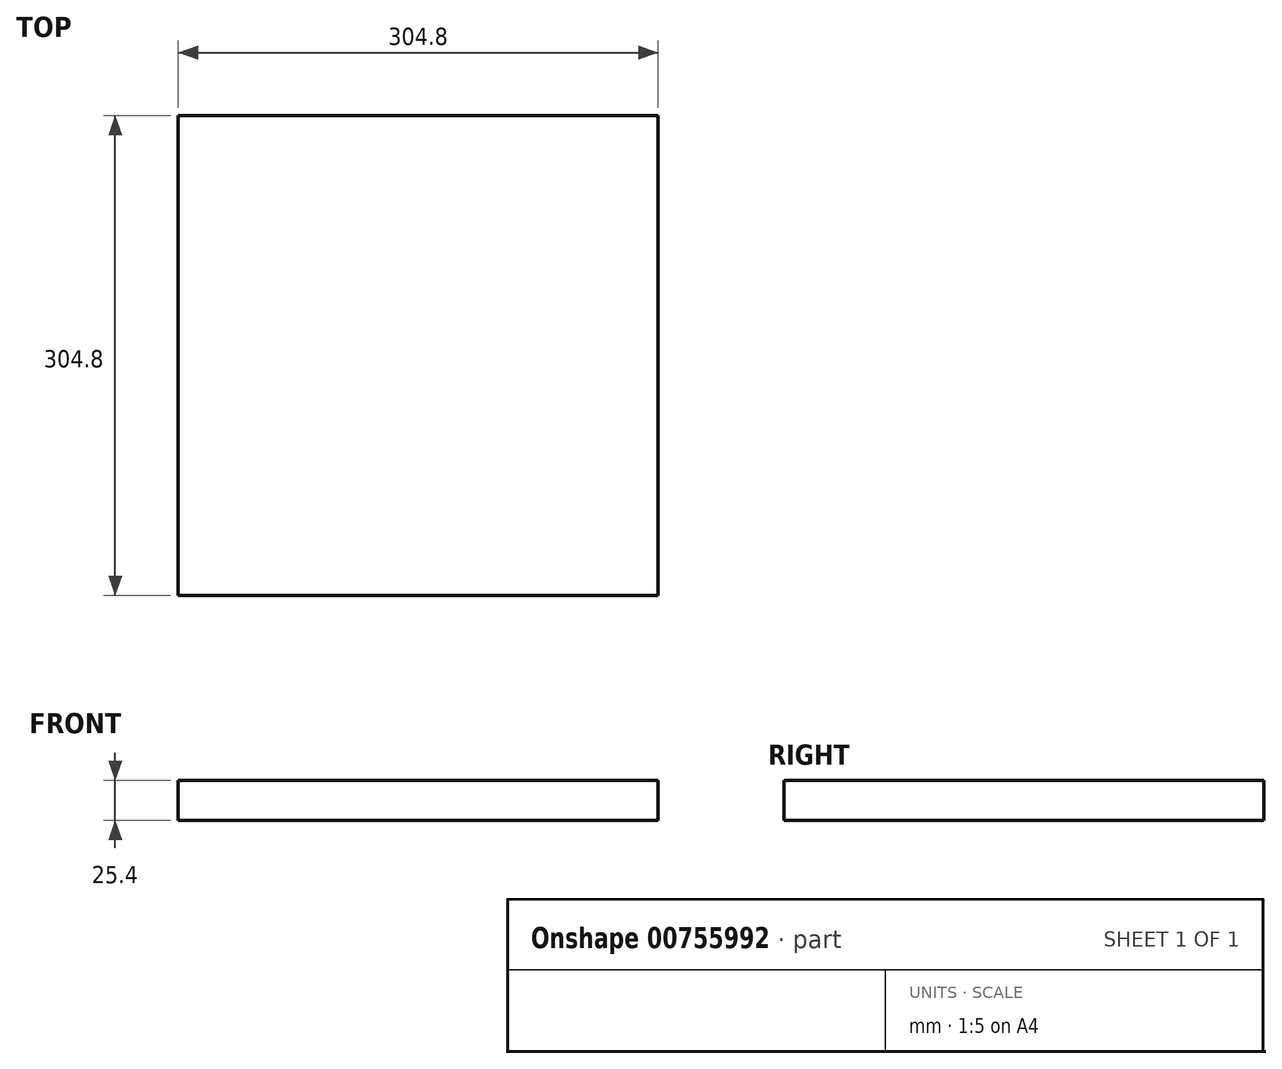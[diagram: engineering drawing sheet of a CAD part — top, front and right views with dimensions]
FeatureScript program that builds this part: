
annotation { "Feature Type Name" : "Feature", "Feature Type Description" : "" }
export const myFeature = defineFeature(function(context is Context, id is Id, definition is map)
    precondition{}
    {
        {
            var Q0;
            Q0=qCreatedBy(makeId("Top.planeOp"),FACE);
            var sketch = newSketch(context, id + "F0", { "sketchPlane" : qUnion([Q0])});
            skLineSegment(sketch, "E0.bottom", {"start": v(152.4, 152.4) * mm, "end": v(-152.4, 152.4) * mm});
            skLineSegment(sketch, "E0.top", {"start": v(152.4, -152.4) * mm, "end": v(-152.4, -152.4) * mm});
            skLineSegment(sketch, "E0.left", {"start": v(152.4, 152.4) * mm, "end": v(152.4, -152.4) * mm});
            skLineSegment(sketch, "E0.right", {"start": v(-152.4, 152.4) * mm, "end": v(-152.4, -152.4) * mm});
            skPoint(sketch, "E0.middle", {"position": v(0, 0) * mm});
            skSolve(sketch);
        }
        {
            var Q0;
            Q0 = qSketchRegion(id + "F0", true);
            extrude(context, id + "F1", {"entities" : qUnion([Q0]), "depth" : 25.4 * mm, "offsetDistance" : 25.4 * mm});
        }
    });
